SOLIDWORKS PART (.sldprt)
format: sldprt  version: not decoded by parser v0  size: 164,864 bytes
history: native  units: mm
features: sketch x3, extrude x3, material x1 (+16 scaffold rows collapsed)
feature tree (23):
  scaffold x16  (default folders/planes/origin — collapsed)
  material  "Material <not specified>"
  sketch  "Sketch1"  dims[D1=2000.0mm D2=4000.0mm D3=1600.0mm D4=1000.0mm D5=1000.0mm D6=1200.0mm D7=1200.0mm D8=1000.0mm]
  extrude  "Extrude1"  Depth=6200mm
  sketch  "Sketch2"  dims[D1=1800.0mm D2=1600.0mm D3=18000.0mm]
  extrude  "Extrude2"  Depth=6200mm
  sketch  "Sketch3"  dims[c1.D1=1000.0mm c1.D2=6000.0mm c1.D3=1000.0mm c1.D4=19000.0mm c1.D5=1000.0mm c1.D6=20000.0mm c1.D7=1600.0mm c1.D8=1700.0mm c1.D9=1700.0mm c2.D8=2200.0mm c2.D9=2200.0mm c2.D10=26000.0mm c3.D8=59000.0mm c3.D9=2000.0mm c3.D11=~2022.697389mm c4.D9=63200.0mm]
  extrude  "Extrude3"  Depth=4500mm
decode coverage: 6 of 6 modeling features carry decoded parameters
note: ~ marks probable driven/reference dimensions
note: suppression state not decoded; provenance and decode notes live in map.json
